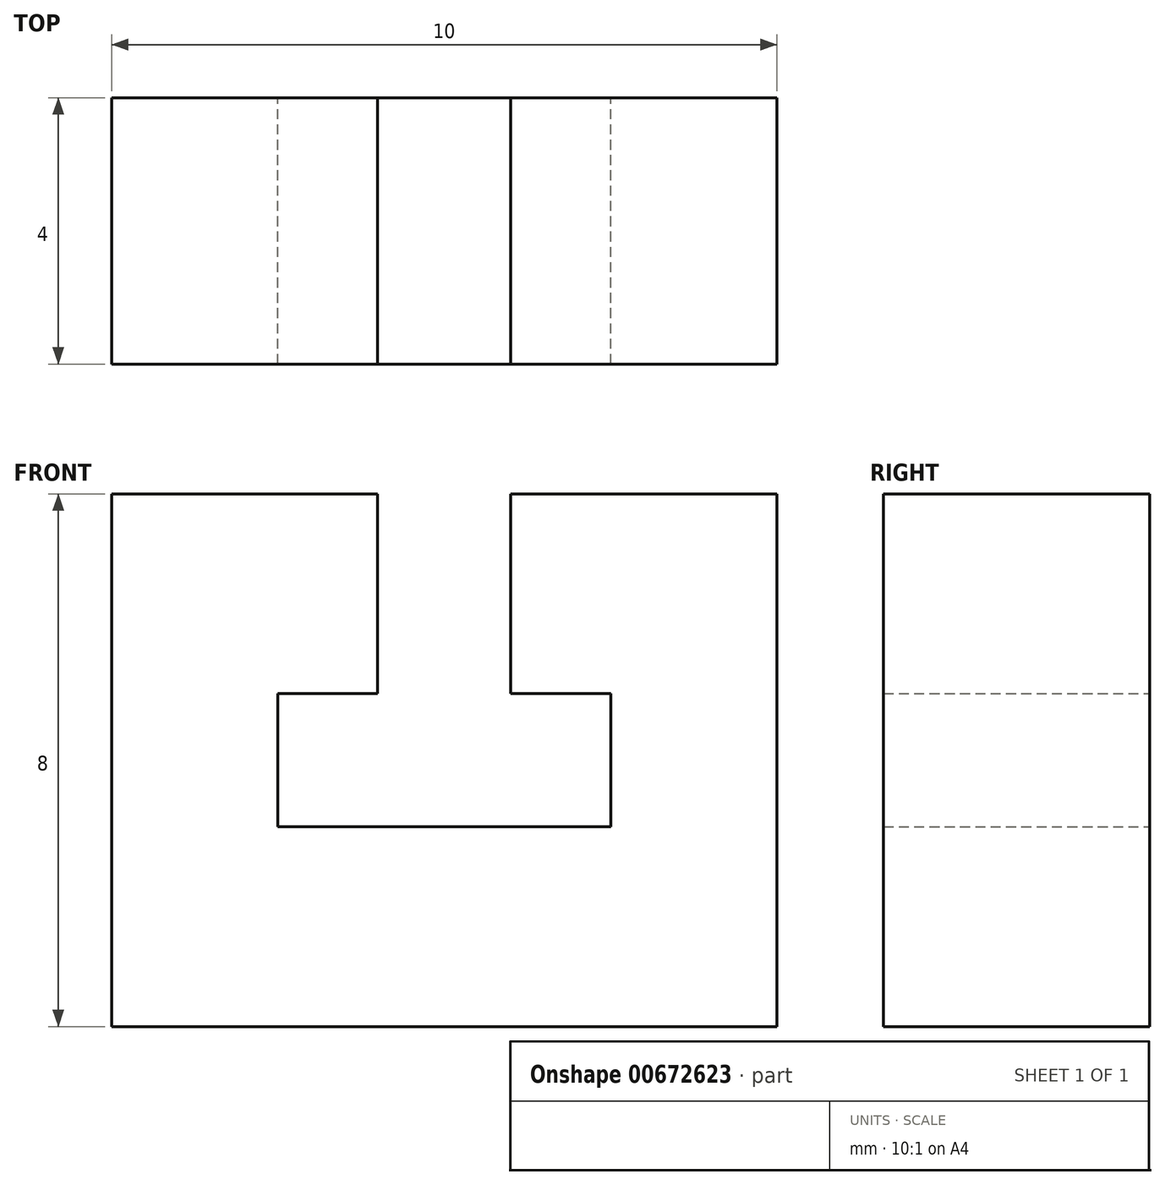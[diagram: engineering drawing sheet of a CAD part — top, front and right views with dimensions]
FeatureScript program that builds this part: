
annotation { "Feature Type Name" : "Feature", "Feature Type Description" : "" }
export const myFeature = defineFeature(function(context is Context, id is Id, definition is map)
    precondition{}
    {
        {
            var Q0;
            Q0=qCreatedBy(makeId("Front.planeOp"),FACE);
            var sketch = newSketch(context, id + "F0", { "sketchPlane" : qUnion([Q0])});
            skLineSegment(sketch, "E0", {"start": v(0, 0) * mm, "end": v(-5, 0) * mm});
            skLineSegment(sketch, "E1", {"start": v(-5, 0) * mm, "end": v(-5, 8) * mm});
            skLineSegment(sketch, "E2", {"start": v(-5, 8) * mm, "end": v(-1, 8) * mm});
            skLineSegment(sketch, "E3", {"start": v(-1, 8) * mm, "end": v(-1, 5) * mm});
            skLineSegment(sketch, "E4", {"start": v(-1, 5) * mm, "end": v(-2.5, 5) * mm});
            skLineSegment(sketch, "E5", {"start": v(-2.5, 5) * mm, "end": v(-2.5, 3) * mm});
            skLineSegment(sketch, "E6", {"start": v(-2.5, 3) * mm, "end": v(0, 3) * mm});
            skLineSegment(sketch, "E7.MirrorCS", {"start": v(0, 0) * mm, "end": v(5, 0) * mm});
            skLineSegment(sketch, "E8.MirrorCS", {"start": v(5, 0) * mm, "end": v(5, 8) * mm});
            skLineSegment(sketch, "E9.MirrorCS", {"start": v(5, 8) * mm, "end": v(1, 8) * mm});
            skLineSegment(sketch, "E10.MirrorCS", {"start": v(1, 8) * mm, "end": v(1, 5) * mm});
            skLineSegment(sketch, "E11.MirrorCS", {"start": v(1, 5) * mm, "end": v(2.5, 5) * mm});
            skLineSegment(sketch, "E12.MirrorCS", {"start": v(2.5, 5) * mm, "end": v(2.5, 3) * mm});
            skLineSegment(sketch, "E13.MirrorCS", {"start": v(2.5, 3) * mm, "end": v(0, 3) * mm});
            skSolve(sketch);
        }
        {
            var Q0;
            Q0=makeQuery(id+"F0.imprint","IMPRINT",FACE,{"disambiguationData":[TD([[makeQuery(id+"F0.imprint","IMPRINT",EDGE,{"derivedFrom":sQuery(id+"F0.wireOp",EDGE,"E0")}),-1.0]])]});
            extrude(context, id + "F1", {"entities" : qUnion([Q0]), "depth" : 4 * mm, "offsetDistance" : 25 * mm});
        }
    });
